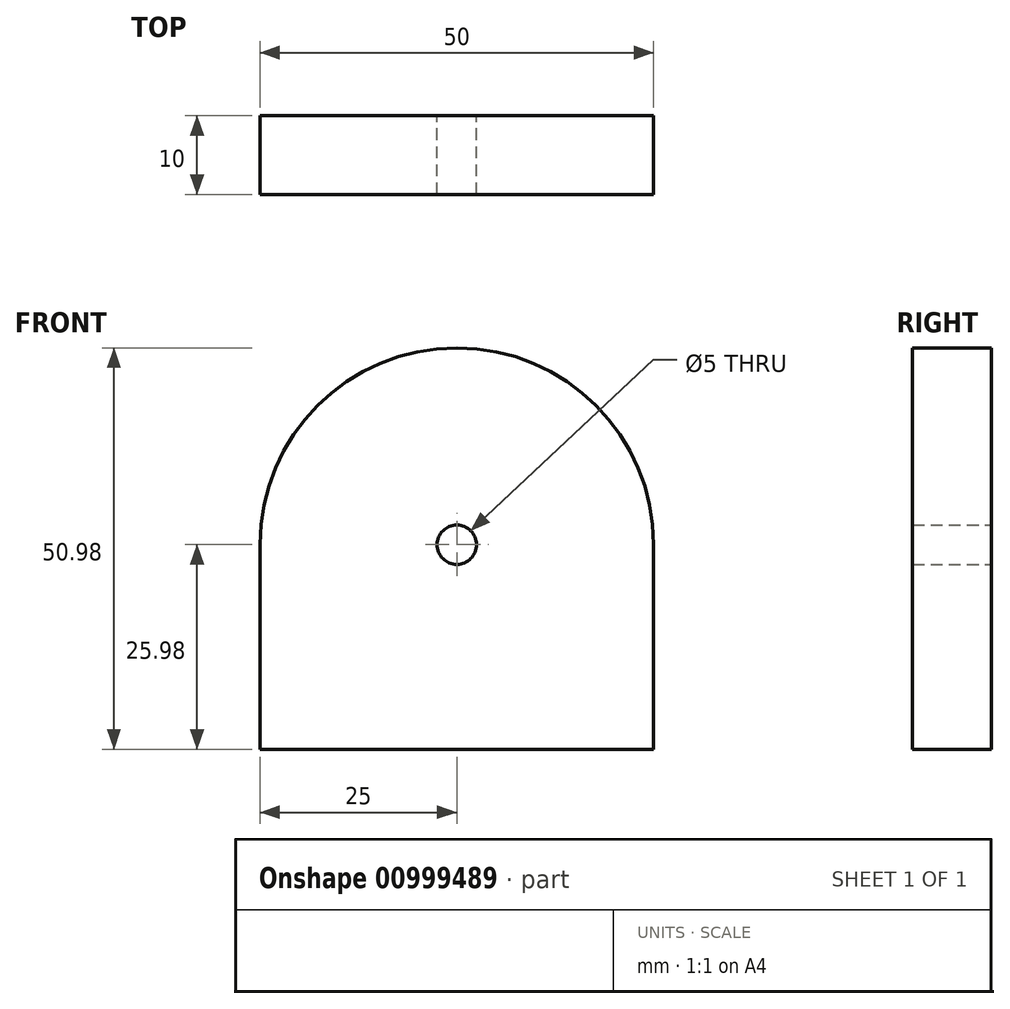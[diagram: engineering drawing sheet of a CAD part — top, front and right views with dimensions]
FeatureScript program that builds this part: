
annotation { "Feature Type Name" : "Feature", "Feature Type Description" : "" }
export const myFeature = defineFeature(function(context is Context, id is Id, definition is map)
    precondition{}
    {
        {
            var Q0;
            Q0=qCreatedBy(makeId("Front.planeOp"),FACE);
            var sketch = newSketch(context, id + "F0", { "sketchPlane" : qUnion([Q0])});
            skCircle(sketch, "E0", {"center": v(0, 0) * mm, "radius": 25 * mm});
            skCircle(sketch, "E1", {"center": v(0, 0) * mm, "radius": 2.5 * mm});
            skLineSegment(sketch, "E2.left", {"start": v(25, 0) * mm, "end": v(25, 0) * mm});
            skLineSegment(sketch, "E2.right", {"start": v(-25, 0) * mm, "end": v(-25, 0) * mm});
            skLineSegment(sketch, "E3.bottom", {"start": v(-25, 0) * mm, "end": v(25, 0) * mm});
            skLineSegment(sketch, "E3.top", {"start": v(-25, -25.98) * mm, "end": v(25, -25.98) * mm});
            skLineSegment(sketch, "E3.left", {"start": v(-25, 0) * mm, "end": v(-25, -25.98) * mm});
            skLineSegment(sketch, "E3.right", {"start": v(25, 0) * mm, "end": v(25, -25.98) * mm});
            skSolve(sketch);
        }
        {
            var Q0;
            Q0=makeQuery(id+"F0.imprint","IMPRINT",FACE,{"disambiguationData":[TD([[makeQuery(id+"F0.imprint","IMPRINT",EDGE,{"derivedFrom":sQuery(id+"F0.wireOp",EDGE,"E3.top")}),1.0]])]});
            var Q1;
            {var subQ0=sQuery(id+"F0.wireOp",EDGE,"E3.bottom");var subQ4=sQuery(id+"F0.wireOp",EDGE,"E1");var subQ6=makeQuery(id+"F0.imprint","INTERSECT",VERTEX,{"disambiguationData":[OD(0.0)],"derivedFrom":[subQ4,subQ0]});Q1=makeQuery(id+"F0.imprint","IMPRINT",FACE,{"disambiguationData":[TD([[makeQuery(id+"F0.imprint","IMPRINT",EDGE,{"disambiguationData":[TD([[subQ6,-1.0]])],"derivedFrom":subQ4}),-1.0]])]});}
            var Q2;
            {var subQ0=sQuery(id+"F0.wireOp",EDGE,"E3.bottom");var subQ4=sQuery(id+"F0.wireOp",EDGE,"E1");var subQ5=makeQuery(id+"F0.imprint","INTERSECT",VERTEX,{"disambiguationData":[OD(0.0)],"derivedFrom":[subQ4,subQ0]});Q2=makeQuery(id+"F0.imprint","IMPRINT",FACE,{"disambiguationData":[TD([[makeQuery(id+"F0.imprint","IMPRINT",EDGE,{"disambiguationData":[TD([[subQ5,1.0]])],"derivedFrom":subQ4}),-1.0]])]});}
            extrude(context, id + "F1", {"entities" : qUnion([Q0, Q1, Q2]), "depth" : 10 * mm, "offsetDistance" : 25 * mm});
        }
    });
